# Revit family: L-industry 30 Turbine
name_source: partatom
category: Осветительные приборы
revit_build: Autodesk Revit 2017 (Build: 20160225_1515(x64)
units: mm (PartAtom-declared; Revit-internal decimal feet)

## family parameters
Всегда вертикально = Да
Источник света = Да
На основе рабочей плоскости = Нет
Общий = Нет
При загрузке вырезать с полостями = Нет
Размер круглого соединителя = Использовать диаметр
Тип детали = Нормальный
Точка расчета площади = Нет

## types (8) — shared parameters
Видимая форма излучения при визуализации = Нет
Изготовитель = LEDEL
Излучение по длине прямоугольника = 250 мм
Излучение по ширине прямоугольника = 44 мм
Классификация нагрузок = Освещение
Комментарии к типоразмеру = Промышленные
Полная установленная мощность = 25 В·А
Светофильтр = 16777215
Смещение цветовой температуры при затухании лампы = <Нет>
Угол наклона = 90.00°

## per-type parameters (varying)
| type | Артикул | Файл фотометрической сетки |
| L-industry 30 Turbine 4.0K Д | 521103000841300 | L-industry 30 Turbine-25-D-4.0K-01.ies |
| L-industry 30 Turbine 5.0K Д | 410012
410012
410012
410010 | L-industry 30 Turbine-25-D-5.0K-01.ies |
| L-industry 30 Turbine 4.0K К15 | 521103002741300 | L-industry 30 Turbine-25-K15-4.0K-01.ies |
| L-industry 30 Turbine 5.0K К15 | 410011 | L-industry 30 Turbine-25-K15-5.0K-01.ies |
| L-industry 30 Turbine 4.0K Г30 | 521103004741300 | L-industry 30 Turbine-25-G30-4.0K-01.ies |
| L-industry 30 Turbine 5.0K Г30 | 410012 | L-industry 30 Turbine-25-G30-5.0K-01.ies |
| L-industry 30 Turbine 4.0K Г60 | 521103006741300 | L-industry 30 Turbine-25-G60-4.0K-01.ies |
| L-industry 30 Turbine 5.0K Г60 | 410013 | L-industry 30 Turbine-25-G60-5.0K-01.ies |
